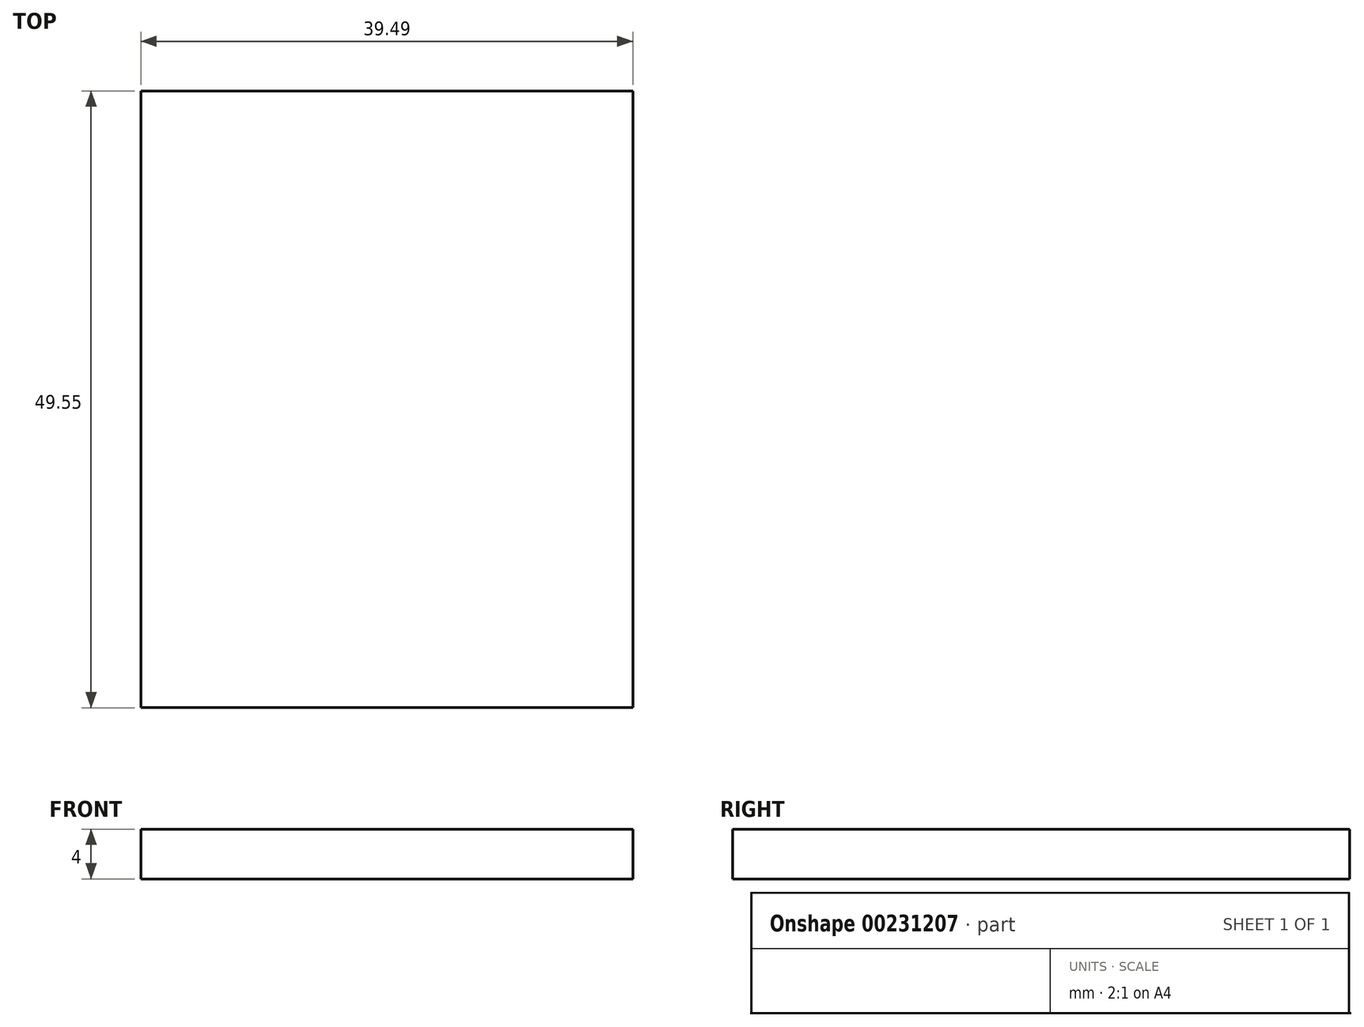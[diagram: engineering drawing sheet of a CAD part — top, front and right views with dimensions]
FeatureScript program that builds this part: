
annotation { "Feature Type Name" : "Feature", "Feature Type Description" : "" }
export const myFeature = defineFeature(function(context is Context, id is Id, definition is map)
    precondition{}
    {
        {
            var Q0;
            Q0=qCreatedBy(makeId("Top.planeOp"),FACE);
            var sketch = newSketch(context, id + "F0", { "sketchPlane" : qUnion([Q0])});
            skLineSegment(sketch, "E0", {"start": v(-82.57, -91.29) * mm, "end": v(-82.57, -41.74) * mm});
            skLineSegment(sketch, "E1", {"start": v(-82.57, -41.74) * mm, "end": v(-43.08, -41.74) * mm});
            skLineSegment(sketch, "E2.bottom", {"start": v(-82.57, -91.29) * mm, "end": v(-43.08, -91.29) * mm});
            skLineSegment(sketch, "E2.right", {"start": v(-43.08, -91.29) * mm, "end": v(-43.08, -41.74) * mm});
            skSolve(sketch);
        }
        {
            var Q0;
            Q0=makeQuery(id+"F0.imprint","IMPRINT",FACE,{"disambiguationData":[TD([[makeQuery(id+"F0.imprint","IMPRINT",EDGE,{"derivedFrom":sQuery(id+"F0.wireOp",EDGE,"E2.bottom")}),1.0]])]});
            extrude(context, id + "F1", {"entities" : qUnion([Q0]), "depth" : 4 * mm});
        }
    });
